# Revit family: 306_3185701e973f4428972ad06911b7d5
name_source: partatom
category: Pipe Accessories
units: mm (PartAtom-declared; Revit-internal decimal feet)

## family parameters
Always vertical = Yes
Cut with Voids When Loaded = No
Part Type = Valve - Breaks Into
Round Connector Dimension = Use Diameter
Shared = No
Work Plane-Based = No

## types (1)
- VTA372 20-55°C G1-3,4
    A = 32 mm
    A1 = 2 mm  [stored 0.00656168 ft]
    A2 = 19 mm
    A3 = 18 mm
    A4 = 14 mm  [stored 0.0459318 ft]
    A5 = 13 mm  [stored 0.0426509 ft]
    A__ve = -32 mm  [stored -0.104987 ft]
    B = 42 mm  [stored 0.137795 ft]
    C = 52 mm  [stored 0.170604 ft]
    CT2 = 21 mm  [stored 0.0688976 ft]
    D = 25 mm
    DT2 = 13 mm  [stored 0.0426509 ft]
    Description = Thermostatic mixing valve VTA372, PN10 external thread
    L2D = 54 mm
    L2D_Min = 3048 mm  [stored 10 ft]
    LT2 = 27 mm  [stored 0.0885827 ft]
    MC = No
    Manufacturer = ESBE
    QmdConnectorList = 301;D;302;D
    R2 = 11 mm  [stored 0.0360892 ft]
    URL = http://www.esbe.eu
    W1 = 17 mm  [stored 0.0557743 ft]
    W2 = 16 mm
    W2D = 25 mm  [stored 0.082021 ft]
    WT2 = 23 mm  [stored 0.0754593 ft]
    X1 = 2 mm  [stored 0.00656168 ft]
    X2 = 8 mm  [stored 0.0262467 ft]
    X3 = 50 mm  [stored 0.164042 ft]
    X4 = 42 mm  [stored 0.137795 ft]
    X7 = 4 mm  [stored 0.0131234 ft]
    X7__ve = -4 mm  [stored -0.0131234 ft]
    Z1 = 3 mm  [stored 0.00984252 ft]
    Z1__ve = -3 mm
    Z2 = 13 mm  [stored 0.0426509 ft]
    Z3 = 5 mm  [stored 0.0164042 ft]
    Z4 = 14 mm  [stored 0.0459318 ft]
    magiPartTypeId = 306
    magiProductCode = VTA372 20-55°C G1-3,4
    magiProductFamilyId = 3185701e973f4428972ad06911b7d5
    magiProductId = d810c9e717244f7ca03812b44c2e3a

note: [stored X ft] marks values corroborated as IEEE doubles in the binary element streams (Revit-internal decimal feet)

## geometry (parser evidence)
native form markers: Sweep x1
no freeform markers — native parametric forms only
